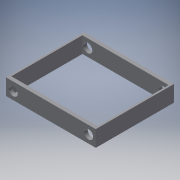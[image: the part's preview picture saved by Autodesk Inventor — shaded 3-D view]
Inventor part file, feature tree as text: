
AUTODESK INVENTOR PART (.ipt)
format: ipt  version: 2018.3 (Build 223284000, 284)  size: 118,272 bytes
history: native  units: mm
features: sketch x4, extrude x3, hole x1
ambient origin geometry x8: Origin, YZ Plane, XZ Plane, XY Plane, X Axis, Y Axis, Z Axis, Center Point
bodies: Solid1 (feature_tree)
feature tree (8):
  extrude  "Extrusion1"  Depth=50.0mm
  extrude  "Extrusion2"  Depth=48.0mm
  extrude  "Extrusion3"  Depth=1.0mm TaperAngle=0.0deg
  hole  "Hole1"  [1 undecoded]
  sketch  "Sketch1"  dims[d0=43.57mm d1=50.0mm]
  sketch  "Sketch2"  dims[d2=41.57mm d3=48.0mm]
  sketch  "Sketch3"  dims[d4=9.0mm d5=0.0mm d6=1.0mm d7=0.0mm]
  sketch  "Sketch4"  dims[d8=1.0mm d9=0.0mm d10=5.0mm d11=6.0mm d12=4.0mm d13=2.0mm d14=90.0deg d15=8.0mm d16=20.594885mm]
note: 1 required parameter value undecoded (feature->parameter linkage not recoverable at this tier; creation-order binding heuristic only, values carry confidence <= 0.55)
